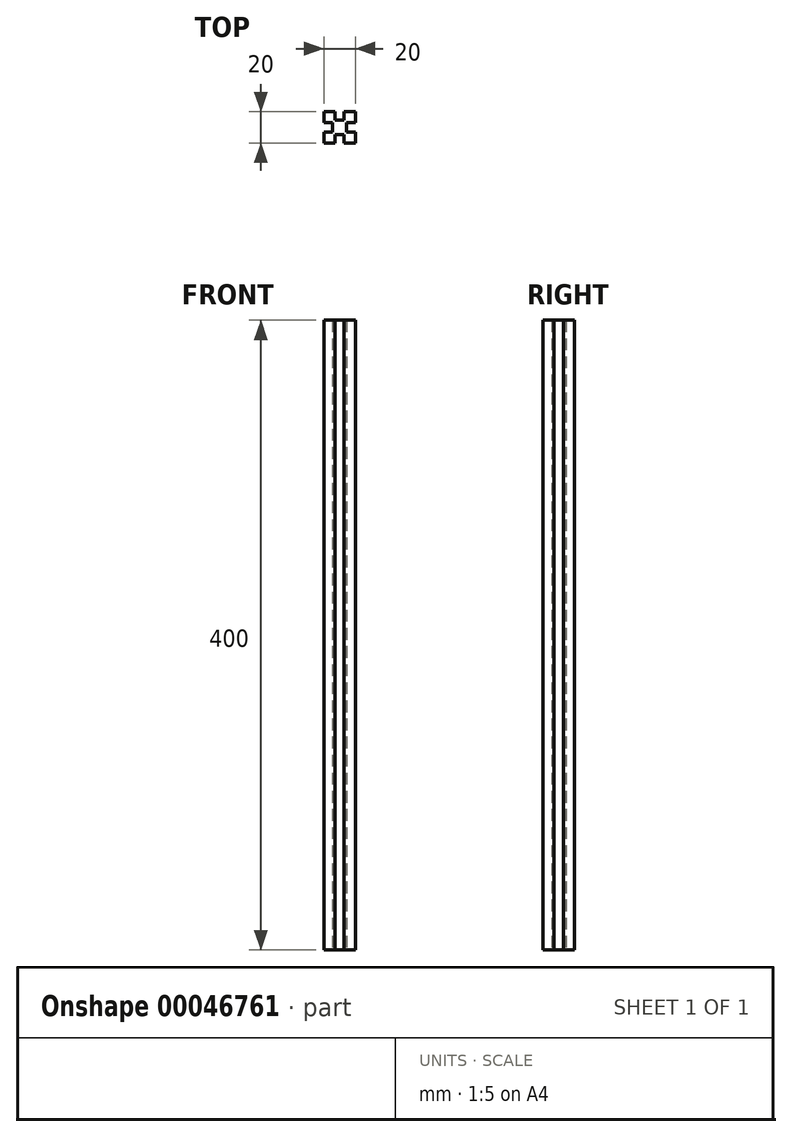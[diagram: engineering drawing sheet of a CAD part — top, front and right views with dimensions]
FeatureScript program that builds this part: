
annotation { "Feature Type Name" : "Feature", "Feature Type Description" : "" }
export const myFeature = defineFeature(function(context is Context, id is Id, definition is map)
    precondition{}
    {
        {
            var Q0;
            Q0=qCreatedBy(makeId("Top.planeOp"),FACE);
            var sketch = newSketch(context, id + "F0", { "sketchPlane" : qUnion([Q0])});
            skLineSegment(sketch, "E0.bottom", {"start": v(0, 0) * mm, "end": v(20, 0) * mm});
            skLineSegment(sketch, "E0.top", {"start": v(0, 20) * mm, "end": v(20, 20) * mm});
            skLineSegment(sketch, "E0.left", {"start": v(0, 0) * mm, "end": v(0, 20) * mm});
            skLineSegment(sketch, "E0.right", {"start": v(20, 0) * mm, "end": v(20, 20) * mm});
            skLineSegment(sketch, "E1.bottom", {"start": v(7, 20) * mm, "end": v(13, 20) * mm});
            skLineSegment(sketch, "E1.top", {"start": v(7, 14.5) * mm, "end": v(13, 14.5) * mm});
            skLineSegment(sketch, "E1.left", {"start": v(7, 20) * mm, "end": v(7, 14.5) * mm});
            skLineSegment(sketch, "E1.right", {"start": v(13, 20) * mm, "end": v(13, 14.5) * mm});
            skLineSegment(sketch, "E2.bottom", {"start": v(20, 13) * mm, "end": v(14.5, 13) * mm});
            skLineSegment(sketch, "E2.top", {"start": v(20, 7) * mm, "end": v(14.5, 7) * mm});
            skLineSegment(sketch, "E2.left", {"start": v(20, 13) * mm, "end": v(20, 7) * mm});
            skLineSegment(sketch, "E2.right", {"start": v(14.5, 13) * mm, "end": v(14.5, 7) * mm});
            skLineSegment(sketch, "E3.bottom", {"start": v(13, 0) * mm, "end": v(7, 0) * mm});
            skLineSegment(sketch, "E3.top", {"start": v(13, 5.5) * mm, "end": v(7, 5.5) * mm});
            skLineSegment(sketch, "E3.left", {"start": v(13, 0) * mm, "end": v(13, 5.5) * mm});
            skLineSegment(sketch, "E3.right", {"start": v(7, 0) * mm, "end": v(7, 5.5) * mm});
            skLineSegment(sketch, "E4.bottom", {"start": v(0, 7) * mm, "end": v(5.5, 7) * mm});
            skLineSegment(sketch, "E4.top", {"start": v(0, 13) * mm, "end": v(5.5, 13) * mm});
            skLineSegment(sketch, "E4.left", {"start": v(0, 7) * mm, "end": v(0, 13) * mm});
            skLineSegment(sketch, "E4.right", {"start": v(5.5, 7) * mm, "end": v(5.5, 13) * mm});
            skSolve(sketch);
        }
        {
            var Q0;
            Q0=makeQuery(id+"F0.imprint","IMPRINT",FACE,{"disambiguationData":[TD([[makeQuery(id+"F0.imprint","IMPRINT",EDGE,{"derivedFrom":sQuery(id+"F0.wireOp",EDGE,"E1.top")}),-1.0]])]});
            extrude(context, id + "F1", {"entities" : qUnion([Q0]), "depth" : 400 * mm});
        }
    });
